# Revit family: M_Downlight - Strip
name_source: partatom
category: Lighting Fixtures
revit_build: Autodesk Revit 2017 (Build: 20160109_1515(x64)
units: mm (PartAtom-declared; Revit-internal decimal feet)

## family parameters
Always vertical = Yes
Cut with Voids When Loaded = No
Light Source = Yes
OmniClass Number = 23.80.70.11.14.11
OmniClass Title = Downlights
Part Type = Normal
Room Calculation Point = No
Round Connector Dimension = Use Diameter
Shared = No
Work Plane-Based = No

## types (4) — shared parameters
Assembly Code = D5020210
Ballast Number of Poles = 1
Color Filter = 16777215
Dimming Lamp Color Temperature Shift = <None>
Fixture Material = Glass, White, High Luminance
Light Box Material = Steel, Paint Finish, Ivory, Glossy
Light Source Symbol Size = 610 mm
Load Classification = Lighting - Dwelling Unit

## per-type parameters (varying)
| type | Apparent Load | Ballast Voltage | Emit from Line Length | Lamp | Light Length | Wattage Comments |
| 1200mm - 120V | 40 VA | 120 V | 1162 mm  [stored 3.81234 ft] | T-12 | 1200 mm | 40 |
| 0600mm - 120V | 17 VA | 120 V | 562 mm  [stored 1.84383 ft] | T-8 | 600 mm | 17 |
| 0600mm - 277V | 17 VA | 277 V | 562 mm  [stored 1.84383 ft] | T-8 | 600 mm | 17 |
| 1200mm - 277V | 40 VA | 277 V | 1162 mm  [stored 3.81234 ft] | T-12 | 1200 mm | 40 |

note: [stored X ft] marks values corroborated as IEEE doubles in the binary element streams (Revit-internal decimal feet)

## geometry (parser evidence)
native form markers: Sweep x1
no freeform markers — native parametric forms only
